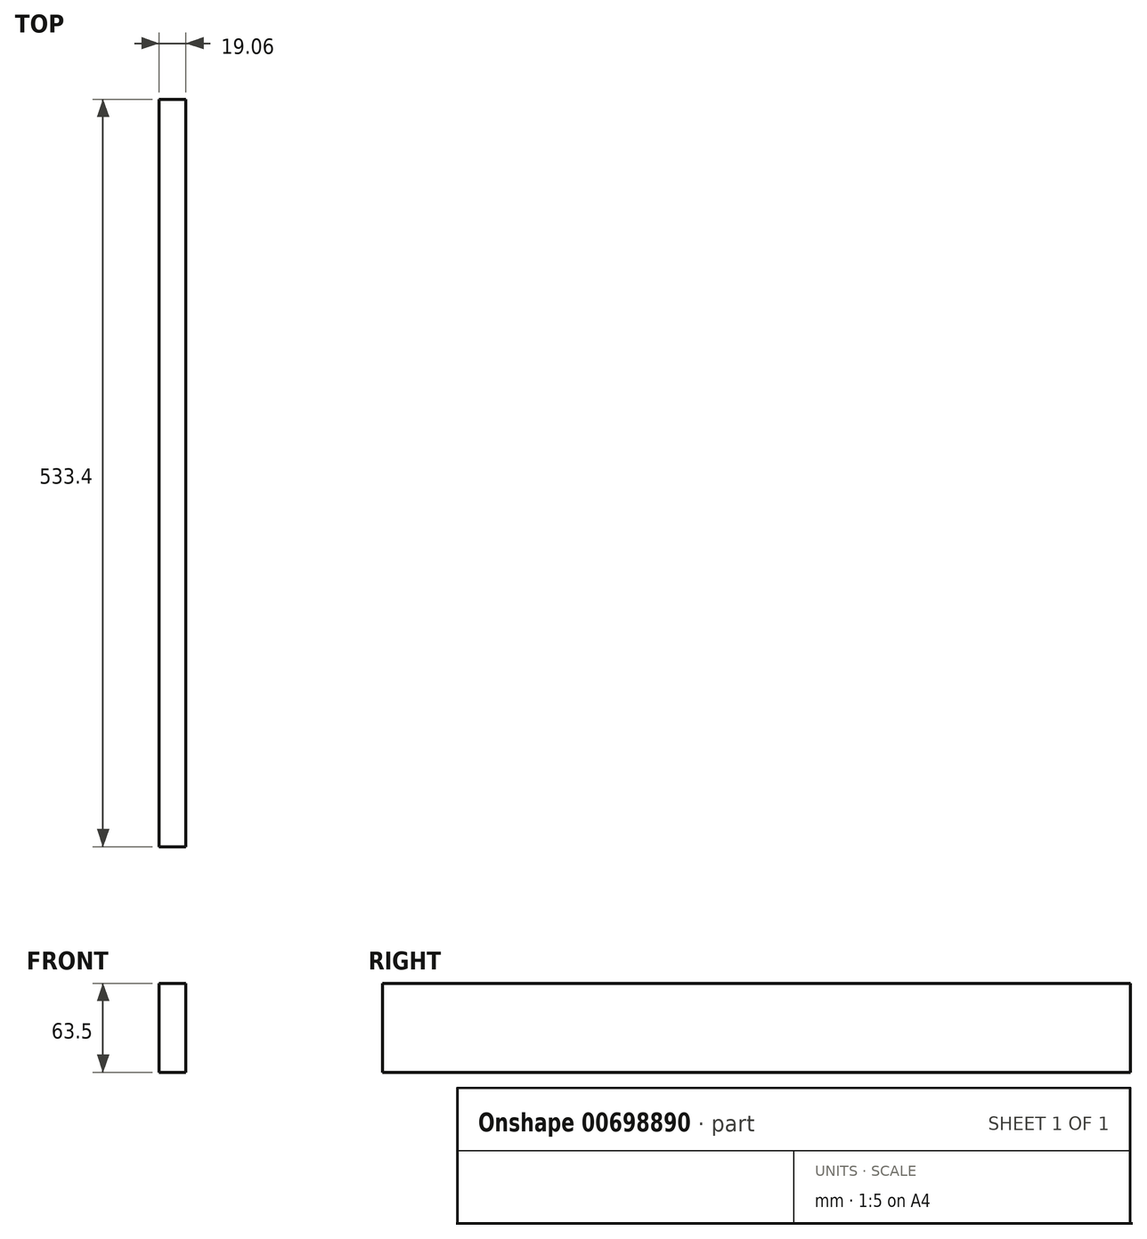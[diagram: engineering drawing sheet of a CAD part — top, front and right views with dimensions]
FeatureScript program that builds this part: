
annotation { "Feature Type Name" : "Feature", "Feature Type Description" : "" }
export const myFeature = defineFeature(function(context is Context, id is Id, definition is map)
    precondition{}
    {
        {
            var Q0;
            Q0=qCreatedBy(makeId("Right.planeOp"),FACE);
            var sketch = newSketch(context, id + "F0", { "sketchPlane" : qUnion([Q0])});
            skLineSegment(sketch, "E0.bottom", {"start": v(266.7, 31.75) * mm, "end": v(-266.7, 31.75) * mm});
            skLineSegment(sketch, "E0.top", {"start": v(266.7, -31.75) * mm, "end": v(-266.7, -31.75) * mm});
            skLineSegment(sketch, "E0.left", {"start": v(266.7, 31.75) * mm, "end": v(266.7, -31.75) * mm});
            skLineSegment(sketch, "E0.right", {"start": v(-266.7, 31.75) * mm, "end": v(-266.7, -31.75) * mm});
            skPoint(sketch, "E0.middle", {"position": v(0, 0) * mm});
            skSolve(sketch);
        }
        {
            var Q0;
            Q0 = qSketchRegion(id + "F0", true);
            extrude(context, id + "F1", {"entities" : qUnion([Q0]), "endBound" : BoundingType.SYMMETRIC, "depth" : 19.05 * mm, "offsetDistance" : 25.4 * mm});
        }
    });
